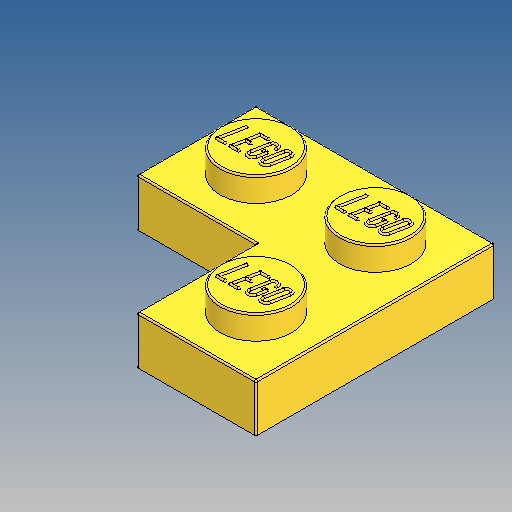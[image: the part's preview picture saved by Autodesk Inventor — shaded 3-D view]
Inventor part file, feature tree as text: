
AUTODESK INVENTOR PART (.ipt)
format: ipt  version: 2025 (Build 290162010, 162A)  size: 2,977,792 bytes
history: native  units: in
note: dims shown in document units (in); Inventor stores cm internally (conversion verified against a paired STEP export)
features: sketch x6, extrude x4, other x3, fillet x2
ambient origin geometry x8: Origin, YZ Plane, XZ Plane, XY Plane, X Axis, Y Axis, Z Axis, Center Point
bodies: Solid1 (feature_tree)
feature tree (15):
  extrude  "Extrusion1"  Depth=0.126in TaperAngle=0.0deg
  extrude  "Extrusion4"  Depth=0.063in TaperAngle=0.0deg
  other  "LEGO:1"
  other  "LEGO:2"
  other  "LEGO:3"
  fillet  "Fillet2"  Radius=0.0039in
  sketch  "Sketch3"  dims[d7=0.0591in d8=0.063in d11=0.063in d12=0.0in d22=0.0039in]
  extrude  "Extrusion2"  Depth=0.189in
  extrude  "Extrusion5"  Depth=0.1575in
  fillet  "Fillet1"  Radius=0.063in
  sketch  "Sketch2"  dims[d0=0.6299in d4=0.126in d5=0.0in]
  sketch  "Sketch9"  dims[d62=0.063in d63=0.189in]
  sketch  "Sketch10"  dims[d64=0.1575in d65=0.1575in d66=0.063in d67=0.0in]
  sketch  "Sketch11"  dims[d68=0.0039in]
  sketch  "Sketch12"  dims[d75=0.315in d77=0.0709in d78=0.0in d91=0.063in d92=0.315in d93=0.0in d94=0.0in d95=0.0in d96=0.0in d97=0.0in d98=0.0in d99=0.6299in d100=0.0in d101=0.0079in d102=0.0732in d103=0.0281in d104=0.035in d105=0.0079in d106=0.0139in d107=0.0281in d108=0.035in d109=0.0281in d110=0.0159in d111=0.0177in d112=0.035in d113=0.5428in d114=0.0079in d115=0.0732in d116=0.0281in d117=0.035in d118=0.0079in d119=0.0139in d120=0.0281in d121=0.035in d122=0.0281in d123=0.0159in d124=0.0177in d125=0.035in d126=0.5428in d127=0.0079in d128=0.0732in d129=0.0281in d130=0.035in d131=0.0079in d132=0.0139in d133=0.0281in d134=0.035in d135=0.0281in d136=0.0159in d137=0.0177in d138=0.035in d139=0.5428in]
